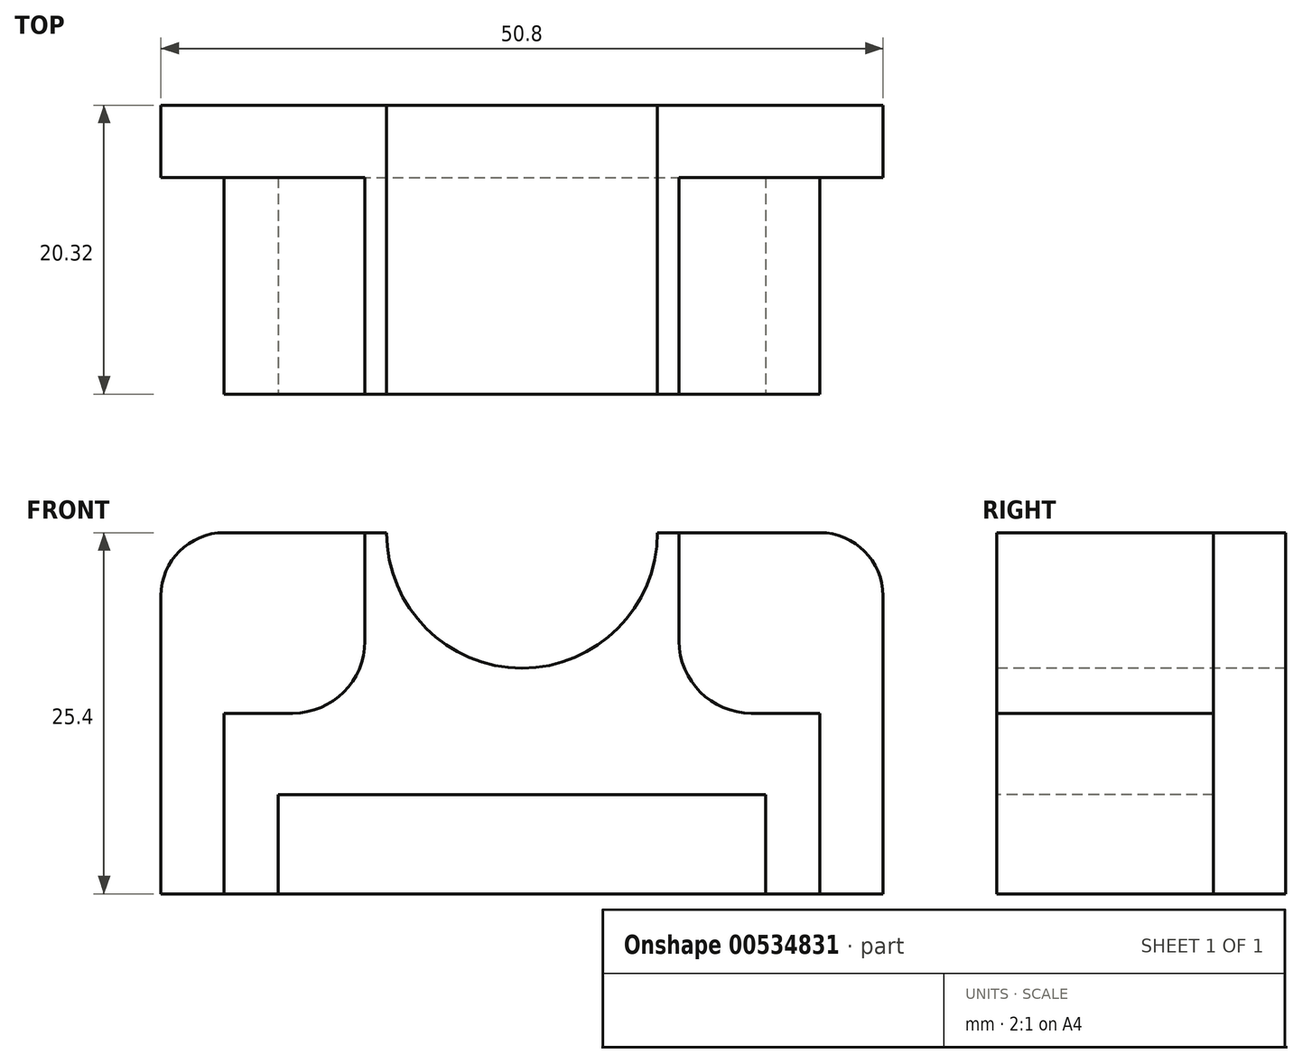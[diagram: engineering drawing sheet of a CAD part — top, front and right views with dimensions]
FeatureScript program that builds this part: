
annotation { "Feature Type Name" : "Feature", "Feature Type Description" : "" }
export const myFeature = defineFeature(function(context is Context, id is Id, definition is map)
    precondition{}
    {
        {
            var Q0;
            Q0=qCreatedBy(makeId("Front.planeOp"),FACE);
            var sketch = newSketch(context, id + "F0", { "sketchPlane" : qUnion([Q0])});
            skLineSegment(sketch, "E0.bottom", {"start": v(-25.4, -12.7) * mm, "end": v(25.4, -12.7) * mm});
            skLineSegment(sketch, "E0.top", {"start": v(-20.96, 12.7) * mm, "end": v(20.96, 12.7) * mm});
            skLineSegment(sketch, "E0.left", {"start": v(-25.4, -12.7) * mm, "end": v(-25.4, 8.26) * mm});
            skLineSegment(sketch, "E0.right", {"start": v(25.4, -12.7) * mm, "end": v(25.4, 8.26) * mm});
            skPoint(sketch, "E0.middle", {"position": v(0, 0) * mm});
            skPoint(sketch, "E1.visualSharp", {"position": v(-25.4, 12.7) * mm});
            skArc(sketch, "E1.filletArc", {"start": v(-20.96, 12.7) * mm, "mid": v(-24.1, 11.4) * mm, "end": v(-25.4, 8.26) * mm});
            skPoint(sketch, "E2.visualSharp", {"position": v(25.4, 12.7) * mm});
            skArc(sketch, "E2.filletArc", {"start": v(25.4, 8.26) * mm, "mid": v(24.1, 11.4) * mm, "end": v(20.96, 12.7) * mm});
            skSolve(sketch);
        }
        {
            var Q0;
            Q0 = qSketchRegion(id + "F0", true);
            extrude(context, id + "F1", {"entities" : qUnion([Q0]), "depth" : 20.32 * mm, "offsetDistance" : 25.4 * mm});
        }
        {
            var Q0;
            Q0=makeQuery(id+"F1.opExtrude","CAP_FACE",FACE,{"disambiguationData":[OSD([sQuery(id+"F0.wireOp",EDGE,"E0.bottom"),sQuery(id+"F0.wireOp",EDGE,"E0.top"),sQuery(id+"F0.wireOp",EDGE,"E0.left"),sQuery(id+"F0.wireOp",EDGE,"E0.right"),sQuery(id+"F0.wireOp",EDGE,"E1.filletArc"),sQuery(id+"F0.wireOp",EDGE,"E2.filletArc")])],"isStart":false});
            var sketch = newSketch(context, id + "F2", { "sketchPlane" : qUnion([Q0])});
            skArc(sketch, "E3", {"start": v(-9.53, 12.7) * mm, "mid": v(0, 3.18) * mm, "end": v(9.52, 12.7) * mm});
            skLineSegment(sketch, "E4", {"start": v(-9.53, 12.7) * mm, "end": v(9.52, 12.7) * mm});
            skSolve(sketch);
        }
        {
            var Q0;
            Q0 = qSketchRegion(id + "F2", true);
            extrude(context, id + "F3", {"entities" : qUnion([Q0]), "operationType" : NewBodyOperationType.REMOVE, "endBound" : BoundingType.THROUGH_ALL, "oppositeDirection" : true, "depth" : 25.4 * mm, "offsetDistance" : 25.4 * mm});
        }
        {
            var Q0;
            Q0=makeQuery(id+"F1.opExtrude","CAP_FACE",FACE,{"disambiguationData":[OSD([sQuery(id+"F0.wireOp",EDGE,"E0.bottom"),sQuery(id+"F0.wireOp",EDGE,"E0.top"),sQuery(id+"F0.wireOp",EDGE,"E0.left"),sQuery(id+"F0.wireOp",EDGE,"E0.right"),sQuery(id+"F0.wireOp",EDGE,"E1.filletArc"),sQuery(id+"F0.wireOp",EDGE,"E2.filletArc")])],"isStart":false});
            var sketch = newSketch(context, id + "F4", { "sketchPlane" : qUnion([Q0])});
            skArc(sketch, "E5.0.0", {"start": v(9.52, 12.7) * mm, "mid": v(0, 3.18) * mm, "end": v(-9.53, 12.7) * mm});
            skLineSegment(sketch, "E5.0.1", {"start": v(-9.53, 12.7) * mm, "end": v(-20.96, 12.7) * mm});
            skArc(sketch, "E5.0.2", {"start": v(-20.96, 12.7) * mm, "mid": v(-24.1, 11.4) * mm, "end": v(-25.4, 8.26) * mm});
            skLineSegment(sketch, "E5.0.3", {"start": v(-25.4, 8.26) * mm, "end": v(-25.4, -12.7) * mm});
            skLineSegment(sketch, "E5.0.4", {"start": v(-25.4, -12.7) * mm, "end": v(25.4, -12.7) * mm});
            skLineSegment(sketch, "E5.0.5", {"start": v(25.4, -12.7) * mm, "end": v(25.4, 8.26) * mm});
            skArc(sketch, "E5.0.6", {"start": v(25.4, 8.26) * mm, "mid": v(24.1, 11.4) * mm, "end": v(20.96, 12.7) * mm});
            skLineSegment(sketch, "E5.0.7", {"start": v(20.96, 12.7) * mm, "end": v(9.52, 12.7) * mm});
            skLineSegment(sketch, "E6", {"start": v(-11.05, 12.7) * mm, "end": v(-11.05, 5.08) * mm});
            skLineSegment(sketch, "E7", {"start": v(-16.13, 0) * mm, "end": v(-20.96, 0) * mm});
            skLineSegment(sketch, "E8", {"start": v(-20.96, 0) * mm, "end": v(-20.96, -12.7) * mm});
            skLineSegment(sketch, "E9", {"start": v(-20.96, -12.7) * mm, "end": v(-17.15, -12.7) * mm});
            skLineSegment(sketch, "E10", {"start": v(-17.15, -12.7) * mm, "end": v(-17.15, -5.71) * mm});
            skLineSegment(sketch, "E11", {"start": v(-17.15, -5.71) * mm, "end": v(0, -5.71) * mm});
            skPoint(sketch, "E12.visualSharp", {"position": v(-11.05, 0) * mm});
            skArc(sketch, "E12.filletArc", {"start": v(-16.13, 0) * mm, "mid": v(-12.54, 1.49) * mm, "end": v(-11.05, 5.08) * mm});
            skLineSegment(sketch, "E13.MirrorCS", {"start": v(11.05, 12.7) * mm, "end": v(11.05, 5.08) * mm});
            skArc(sketch, "E14.MirrorCS", {"start": v(16.13, 0) * mm, "mid": v(12.54, 1.49) * mm, "end": v(11.05, 5.08) * mm});
            skLineSegment(sketch, "E15.MirrorCS", {"start": v(16.13, 0) * mm, "end": v(20.96, 0) * mm});
            skLineSegment(sketch, "E16.MirrorCS", {"start": v(20.96, 0) * mm, "end": v(20.96, -12.7) * mm});
            skLineSegment(sketch, "E17.MirrorCS", {"start": v(17.15, -12.7) * mm, "end": v(17.15, -5.71) * mm});
            skLineSegment(sketch, "E18.MirrorCS", {"start": v(17.15, -5.71) * mm, "end": v(0, -5.71) * mm});
            skSolve(sketch);
        }
        {
            var Q0;
            {var subQ3=sQuery(id+"F4.wireOp",EDGE,"E5.0.2");Q0=makeQuery(id+"F4.imprint","IMPRINT",FACE,{"disambiguationData":[TD([[makeQuery(id+"F4.imprint","IMPRINT",EDGE,{"derivedFrom":subQ3}),1.0]])]});}
            var Q1;
            {var subQ1=sQuery(id+"F4.wireOp",EDGE,"E10");Q1=makeQuery(id+"F4.imprint","IMPRINT",FACE,{"disambiguationData":[TD([[makeQuery(id+"F4.imprint","IMPRINT",EDGE,{"derivedFrom":subQ1}),-1.0]])]});}
            var Q2;
            {var subQ4=sQuery(id+"F4.wireOp",EDGE,"E5.0.5");Q2=makeQuery(id+"F4.imprint","IMPRINT",FACE,{"disambiguationData":[TD([[makeQuery(id+"F4.imprint","IMPRINT",EDGE,{"derivedFrom":subQ4}),1.0]])]});}
            extrude(context, id + "F5", {"entities" : qUnion([Q0, Q1, Q2]), "operationType" : NewBodyOperationType.REMOVE, "oppositeDirection" : true, "depth" : 15.24 * mm, "offsetDistance" : 25.4 * mm});
        }
    });
